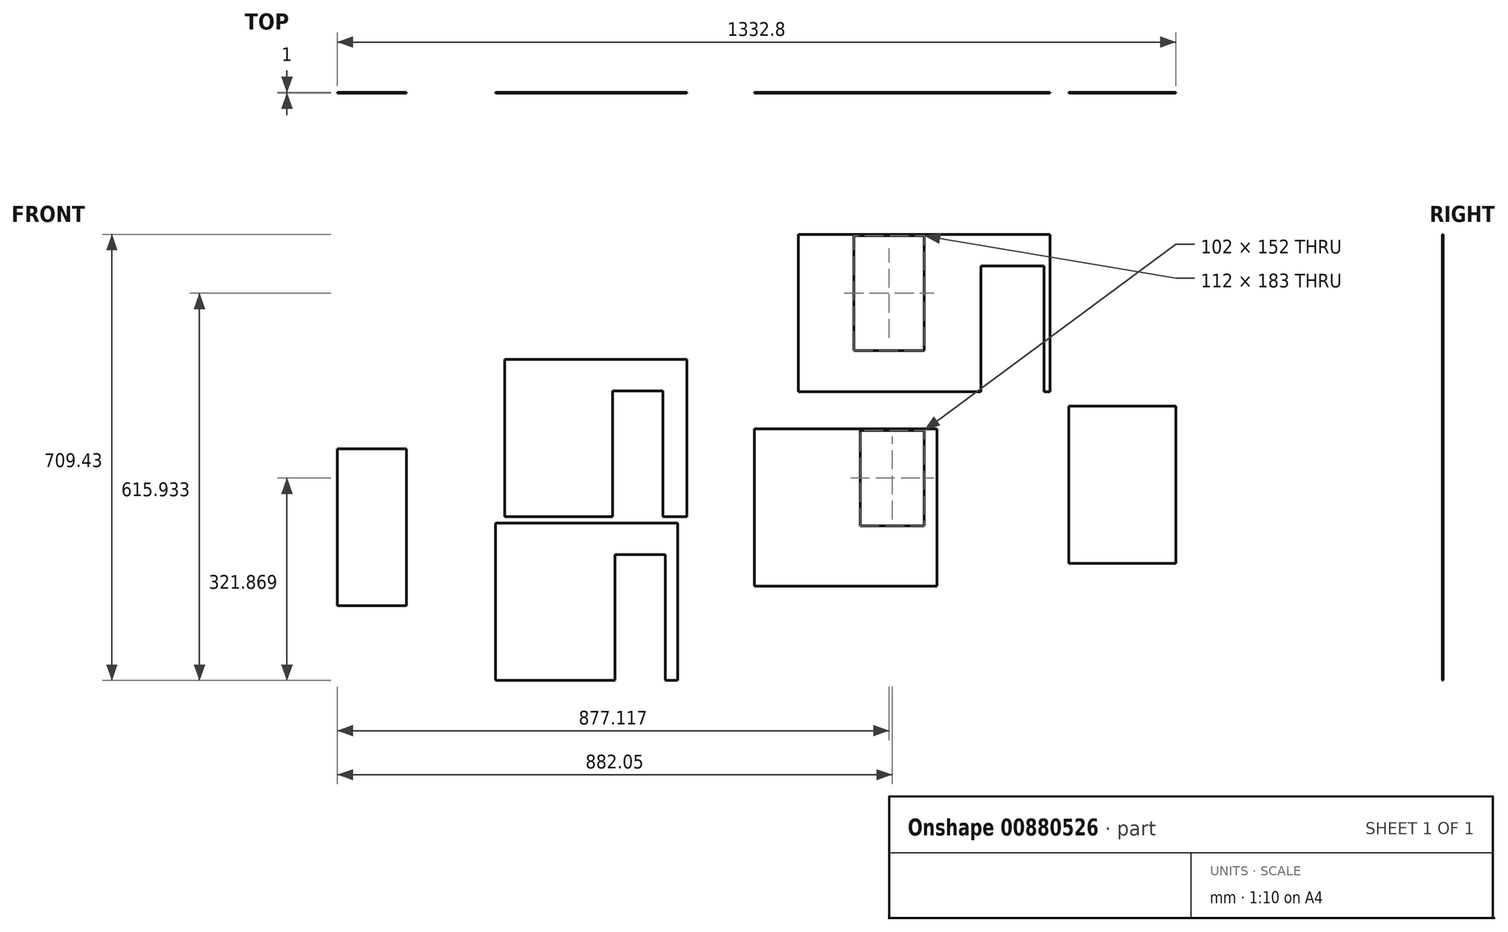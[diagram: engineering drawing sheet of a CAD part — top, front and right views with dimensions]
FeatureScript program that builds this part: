
annotation { "Feature Type Name" : "Feature", "Feature Type Description" : "" }
export const myFeature = defineFeature(function(context is Context, id is Id, definition is map)
    precondition{}
    {
        {
            var Q0;
            Q0=qCreatedBy(makeId("Front.planeOp"),FACE);
            var sketch = newSketch(context, id + "F0", { "sketchPlane" : qUnion([Q0])});
            skLineSegment(sketch, "E0.bottom", {"start": v(-199.93, 397.3) * mm, "end": v(200.07, 397.3) * mm});
            skLineSegment(sketch, "E0.top", {"start": v(-199.93, 147.3) * mm, "end": v(200.07, 147.3) * mm});
            skLineSegment(sketch, "E0.left", {"start": v(-199.93, 397.3) * mm, "end": v(-199.93, 147.3) * mm});
            skLineSegment(sketch, "E0.right", {"start": v(200.07, 397.3) * mm, "end": v(200.07, 147.3) * mm});
            skLineSegment(sketch, "E1.bottom", {"start": v(-667.22, 198.3) * mm, "end": v(-377.22, 198.3) * mm});
            skLineSegment(sketch, "E1.top", {"start": v(-667.22, -51.7) * mm, "end": v(-377.22, -51.7) * mm});
            skLineSegment(sketch, "E1.left", {"start": v(-667.22, 198.3) * mm, "end": v(-667.22, -51.7) * mm});
            skLineSegment(sketch, "E1.right", {"start": v(-377.22, 198.3) * mm, "end": v(-377.22, -51.7) * mm});
            skLineSegment(sketch, "E2.bottom", {"start": v(-681.77, -62.14) * mm, "end": v(-391.77, -62.14) * mm});
            skLineSegment(sketch, "E2.top", {"start": v(-681.77, -312.14) * mm, "end": v(-391.77, -312.14) * mm});
            skLineSegment(sketch, "E2.left", {"start": v(-681.77, -62.14) * mm, "end": v(-681.77, -312.14) * mm});
            skLineSegment(sketch, "E2.right", {"start": v(-391.77, -62.14) * mm, "end": v(-391.77, -312.14) * mm});
            skLineSegment(sketch, "E3.bottom", {"start": v(-270, 87.73) * mm, "end": v(20, 87.73) * mm});
            skLineSegment(sketch, "E3.top", {"start": v(-270, -162.27) * mm, "end": v(20, -162.27) * mm});
            skLineSegment(sketch, "E3.left", {"start": v(-270, 87.73) * mm, "end": v(-270, -162.27) * mm});
            skLineSegment(sketch, "E3.right", {"start": v(20, 87.73) * mm, "end": v(20, -162.27) * mm});
            skLineSegment(sketch, "E4.bottom", {"start": v(229.75, 124.1) * mm, "end": v(399.75, 124.1) * mm});
            skLineSegment(sketch, "E4.top", {"start": v(229.75, -125.9) * mm, "end": v(399.75, -125.9) * mm});
            skLineSegment(sketch, "E4.left", {"start": v(229.75, 124.1) * mm, "end": v(229.75, -125.9) * mm});
            skLineSegment(sketch, "E4.right", {"start": v(399.75, 124.1) * mm, "end": v(399.75, -125.9) * mm});
            skLineSegment(sketch, "E5", {"start": v(190.07, 147.3) * mm, "end": v(190.07, 347.3) * mm});
            skLineSegment(sketch, "E6", {"start": v(190.07, 347.3) * mm, "end": v(90.07, 347.3) * mm});
            skLineSegment(sketch, "E7", {"start": v(90.07, 347.3) * mm, "end": v(90.07, 147.3) * mm});
            skLineSegment(sketch, "E8.bottom", {"start": v(0.07, 395.3) * mm, "end": v(-111.93, 395.3) * mm});
            skLineSegment(sketch, "E8.top", {"start": v(0.07, 212.3) * mm, "end": v(-111.93, 212.3) * mm});
            skLineSegment(sketch, "E8.left", {"start": v(0.07, 395.3) * mm, "end": v(0.07, 212.3) * mm});
            skLineSegment(sketch, "E8.right", {"start": v(-111.93, 395.3) * mm, "end": v(-111.93, 212.3) * mm});
            skLineSegment(sketch, "E9", {"start": v(-415.22, -51.7) * mm, "end": v(-415.22, 148.3) * mm});
            skLineSegment(sketch, "E10", {"start": v(-415.22, 148.3) * mm, "end": v(-495.22, 148.3) * mm});
            skLineSegment(sketch, "E11", {"start": v(-495.22, 148.3) * mm, "end": v(-495.22, -51.7) * mm});
            skLineSegment(sketch, "E12", {"start": v(-411.77, -312.14) * mm, "end": v(-411.77, -112.14) * mm});
            skLineSegment(sketch, "E13", {"start": v(-411.77, -112.14) * mm, "end": v(-491.77, -112.14) * mm});
            skLineSegment(sketch, "E14", {"start": v(-491.77, -112.14) * mm, "end": v(-491.77, -312.14) * mm});
            skLineSegment(sketch, "E15.bottom", {"start": v(-102, 85.73) * mm, "end": v(0, 85.73) * mm});
            skLineSegment(sketch, "E15.top", {"start": v(-102, -66.27) * mm, "end": v(0, -66.27) * mm});
            skLineSegment(sketch, "E15.left", {"start": v(-102, 85.73) * mm, "end": v(-102, -66.27) * mm});
            skLineSegment(sketch, "E15.right", {"start": v(0, 85.73) * mm, "end": v(0, -66.27) * mm});
            skSolve(sketch);
        }
        {
            var Q0;
            Q0=makeQuery(id+"F0.imprint","IMPRINT",FACE,{"disambiguationData":[TD([[makeQuery(id+"F0.imprint","IMPRINT",EDGE,{"derivedFrom":sQuery(id+"F0.wireOp",EDGE,"E1.bottom")}),-1.0]])]});
            var Q1;
            Q1=makeQuery(id+"F0.imprint","IMPRINT",FACE,{"disambiguationData":[TD([[makeQuery(id+"F0.imprint","IMPRINT",EDGE,{"derivedFrom":sQuery(id+"F0.wireOp",EDGE,"E2.bottom")}),-1.0]])]});
            var Q2;
            Q2=makeQuery(id+"F0.imprint","IMPRINT",FACE,{"disambiguationData":[TD([[makeQuery(id+"F0.imprint","IMPRINT",EDGE,{"derivedFrom":sQuery(id+"F0.wireOp",EDGE,"E0.bottom")}),-1.0]])]});
            var Q3;
            Q3=makeQuery(id+"F0.imprint","IMPRINT",FACE,{"disambiguationData":[TD([[makeQuery(id+"F0.imprint","IMPRINT",EDGE,{"derivedFrom":sQuery(id+"F0.wireOp",EDGE,"E3.bottom")}),-1.0]])]});
            var Q4;
            Q4=makeQuery(id+"F0.imprint","IMPRINT",FACE,{"disambiguationData":[TD([[makeQuery(id+"F0.imprint","IMPRINT",EDGE,{"derivedFrom":sQuery(id+"F0.wireOp",EDGE,"E4.bottom")}),-1.0]])]});
            extrude(context, id + "F1", {"entities" : qUnion([Q0, Q1, Q2, Q3, Q4]), "depth" : 1 * mm, "offsetDistance" : 25 * mm});
        }
        {
            var Q0;
            Q0=qCreatedBy(makeId("Front.planeOp"),FACE);
            var sketch = newSketch(context, id + "F2", { "sketchPlane" : qUnion([Q0])});
            skLineSegment(sketch, "E16.bottom", {"start": v(-933.05, 56.4) * mm, "end": v(-823.05, 56.4) * mm});
            skLineSegment(sketch, "E16.top", {"start": v(-933.05, -193.6) * mm, "end": v(-823.05, -193.6) * mm});
            skLineSegment(sketch, "E16.left", {"start": v(-933.05, 56.4) * mm, "end": v(-933.05, -193.6) * mm});
            skLineSegment(sketch, "E16.right", {"start": v(-823.05, 56.4) * mm, "end": v(-823.05, -193.6) * mm});
            skSolve(sketch);
        }
        {
            var Q0;
            Q0=makeQuery(id+"F2.imprint","IMPRINT",FACE,{"disambiguationData":[TD([[makeQuery(id+"F2.imprint","IMPRINT",EDGE,{"derivedFrom":sQuery(id+"F2.wireOp",EDGE,"E16.bottom")}),-1.0]])]});
            extrude(context, id + "F3", {"entities" : qUnion([Q0]), "depth" : 1 * mm, "offsetDistance" : 25 * mm});
        }
    });
